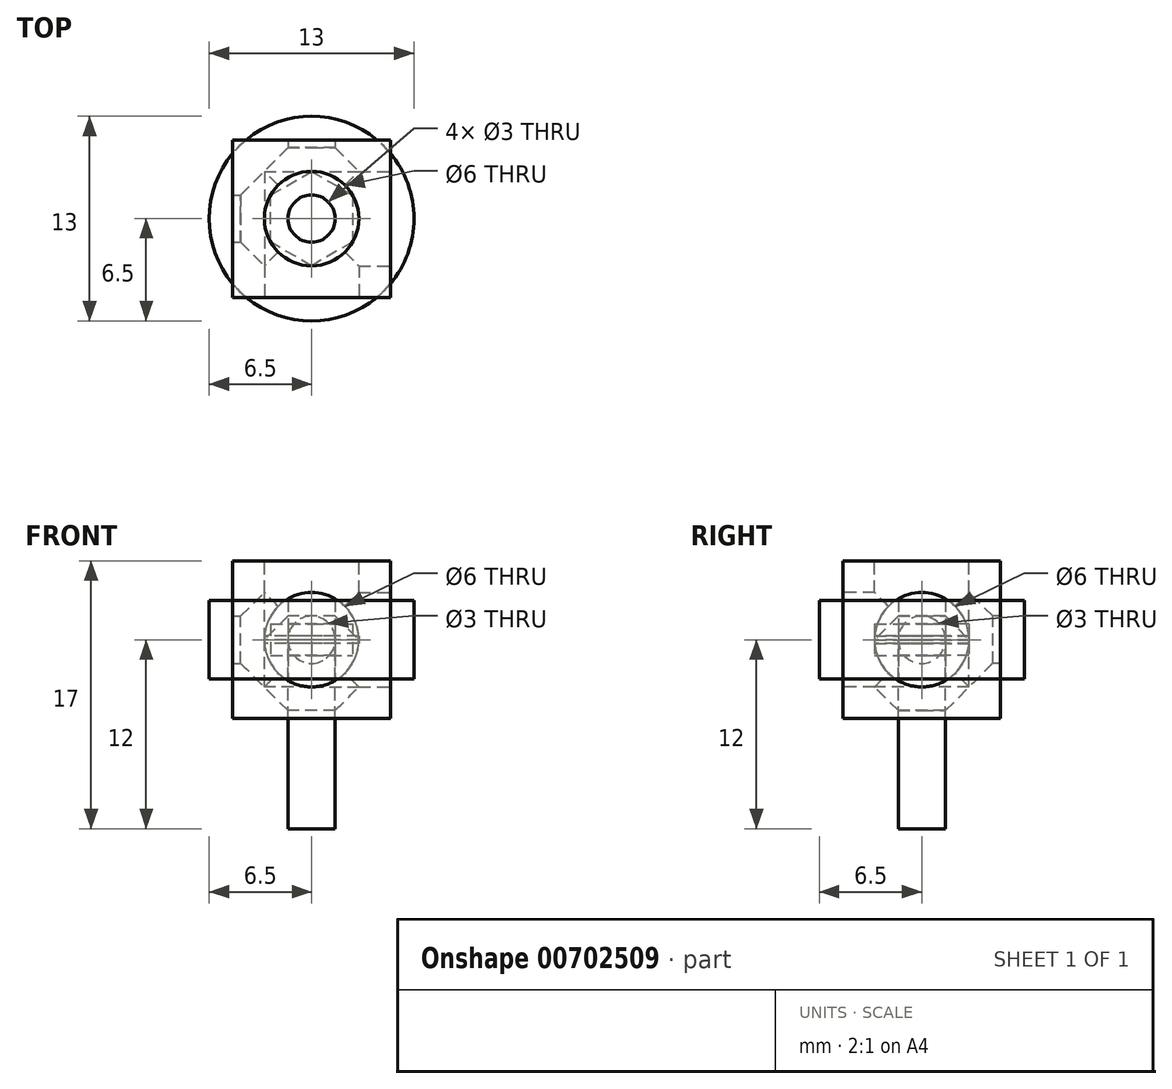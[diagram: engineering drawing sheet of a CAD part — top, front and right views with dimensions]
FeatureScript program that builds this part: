
annotation { "Feature Type Name" : "Feature", "Feature Type Description" : "" }
export const myFeature = defineFeature(function(context is Context, id is Id, definition is map)
    precondition{}
    {
        {
            var Q0;
            Q0=qCreatedBy(makeId("Top.planeOp"),FACE);
            var sketch = newSketch(context, id + "F0", { "sketchPlane" : qUnion([Q0])});
            skLineSegment(sketch, "E0.bottom", {"start": v(-5, 5) * mm, "end": v(5, 5) * mm});
            skLineSegment(sketch, "E0.top", {"start": v(-5, -5) * mm, "end": v(5, -5) * mm});
            skLineSegment(sketch, "E0.left", {"start": v(-5, 5) * mm, "end": v(-5, -5) * mm});
            skLineSegment(sketch, "E0.right", {"start": v(5, 5) * mm, "end": v(5, -5) * mm});
            skPoint(sketch, "E0.middle", {"position": v(0, 0) * mm});
            skSolve(sketch);
        }
        {
            var Q0;
            Q0=makeQuery(id+"F0.imprint","IMPRINT",FACE,{"disambiguationData":[TD([[makeQuery(id+"F0.imprint","IMPRINT",EDGE,{"derivedFrom":sQuery(id+"F0.wireOp",EDGE,"E0.bottom")}),-1.0]])]});
            extrude(context, id + "F1", {"entities" : qUnion([Q0]), "endBound" : BoundingType.SYMMETRIC, "depth" : 10 * mm, "offsetDistance" : 25 * mm});
        }
        {
            var Q0;
            Q0=makeQuery(id+"F1.opExtrude","SWEPT_FACE",FACE,{"disambiguationData":[OSD([sQuery(id+"F0.wireOp",EDGE,"E0.top")])]});
            var sketch = newSketch(context, id + "F2", { "sketchPlane" : qUnion([Q0])});
            skCircle(sketch, "E1", {"center": v(0, 0) * mm, "radius": 3 * mm});
            skCircle(sketch, "E2", {"center": v(0, 0) * mm, "radius": 1.5 * mm});
            skSolve(sketch);
        }
        {
            var Q0;
            Q0=makeQuery(id+"F2.imprint","IMPRINT",FACE,{"disambiguationData":[TD([[makeQuery(id+"F2.imprint","IMPRINT",EDGE,{"derivedFrom":sQuery(id+"F2.wireOp",EDGE,"E1")}),1.0]])]});
            var Q1;
            Q1=makeQuery(id+"F2.imprint","IMPRINT",FACE,{"disambiguationData":[TD([[makeQuery(id+"F2.imprint","IMPRINT",EDGE,{"derivedFrom":sQuery(id+"F2.wireOp",EDGE,"E2")}),1.0]])]});
            extrude(context, id + "F3", {"entities" : qUnion([Q0, Q1]), "operationType" : NewBodyOperationType.REMOVE, "oppositeDirection" : true, "depth" : 8 * mm, "offsetDistance" : 25 * mm});
        }
        {
            var Q0;
            Q0=makeQuery(id+"F1.opExtrude","SWEPT_FACE",FACE,{"disambiguationData":[OSD([sQuery(id+"F0.wireOp",EDGE,"E0.right")])]});
            var sketch = newSketch(context, id + "F4", { "sketchPlane" : qUnion([Q0])});
            skCircle(sketch, "E3", {"center": v(0, 0) * mm, "radius": 3 * mm});
            skCircle(sketch, "E4", {"center": v(0, 0) * mm, "radius": 1.5 * mm});
            skSolve(sketch);
        }
        {
            var Q0;
            Q0=makeQuery(id+"F4.imprint","IMPRINT",FACE,{"disambiguationData":[TD([[makeQuery(id+"F4.imprint","IMPRINT",EDGE,{"derivedFrom":sQuery(id+"F4.wireOp",EDGE,"E3")}),1.0]])]});
            var Q1;
            Q1=makeQuery(id+"F4.imprint","IMPRINT",FACE,{"disambiguationData":[TD([[makeQuery(id+"F4.imprint","IMPRINT",EDGE,{"derivedFrom":sQuery(id+"F4.wireOp",EDGE,"E4")}),1.0]])]});
            extrude(context, id + "F5", {"entities" : qUnion([Q0, Q1]), "operationType" : NewBodyOperationType.REMOVE, "oppositeDirection" : true, "depth" : 8 * mm, "offsetDistance" : 25 * mm});
        }
        {
            var Q0;
            Q0=makeQuery(id+"F1.opExtrude","CAP_FACE",FACE,{"disambiguationData":[OSD([sQuery(id+"F0.wireOp",EDGE,"E0.bottom"),sQuery(id+"F0.wireOp",EDGE,"E0.top"),sQuery(id+"F0.wireOp",EDGE,"E0.left"),sQuery(id+"F0.wireOp",EDGE,"E0.right")])],"isStart":false});
            var sketch = newSketch(context, id + "F6", { "sketchPlane" : qUnion([Q0])});
            skCircle(sketch, "E5", {"center": v(0, 0) * mm, "radius": 3 * mm});
            skCircle(sketch, "E6", {"center": v(0, 0) * mm, "radius": 1.5 * mm});
            skSolve(sketch);
        }
        {
            var Q0;
            Q0=makeQuery(id+"F6.imprint","IMPRINT",FACE,{"disambiguationData":[TD([[makeQuery(id+"F6.imprint","IMPRINT",EDGE,{"derivedFrom":sQuery(id+"F6.wireOp",EDGE,"E5")}),1.0]])]});
            var Q1;
            Q1=makeQuery(id+"F6.imprint","IMPRINT",FACE,{"disambiguationData":[TD([[makeQuery(id+"F6.imprint","IMPRINT",EDGE,{"derivedFrom":sQuery(id+"F6.wireOp",EDGE,"E6")}),1.0]])]});
            extrude(context, id + "F7", {"entities" : qUnion([Q0, Q1]), "operationType" : NewBodyOperationType.REMOVE, "oppositeDirection" : true, "depth" : 8 * mm, "offsetDistance" : 25 * mm});
        }
        {
            var Q0;
            Q0=makeQuery(id+"F2.imprint","IMPRINT",FACE,{"disambiguationData":[TD([[makeQuery(id+"F2.imprint","IMPRINT",EDGE,{"derivedFrom":sQuery(id+"F2.wireOp",EDGE,"E2")}),1.0]])]});
            extrude(context, id + "F8", {"entities" : qUnion([Q0]), "operationType" : NewBodyOperationType.REMOVE, "endBound" : BoundingType.THROUGH_ALL, "oppositeDirection" : true, "depth" : 25 * mm, "offsetDistance" : 25 * mm});
        }
        {
            var Q0;
            Q0=makeQuery(id+"F4.imprint","IMPRINT",FACE,{"disambiguationData":[TD([[makeQuery(id+"F4.imprint","IMPRINT",EDGE,{"derivedFrom":sQuery(id+"F4.wireOp",EDGE,"E4")}),1.0]])]});
            extrude(context, id + "F9", {"entities" : qUnion([Q0]), "operationType" : NewBodyOperationType.REMOVE, "endBound" : BoundingType.THROUGH_ALL, "oppositeDirection" : true, "depth" : 25 * mm, "offsetDistance" : 25 * mm});
        }
        {
            var Q0;
            Q0=makeQuery(id+"F6.imprint","IMPRINT",FACE,{"disambiguationData":[TD([[makeQuery(id+"F6.imprint","IMPRINT",EDGE,{"derivedFrom":sQuery(id+"F6.wireOp",EDGE,"E6")}),1.0]])]});
            extrude(context, id + "F10", {"entities" : qUnion([Q0]), "operationType" : NewBodyOperationType.REMOVE, "endBound" : BoundingType.THROUGH_ALL, "oppositeDirection" : true, "depth" : 25 * mm, "offsetDistance" : 25 * mm});
        }
        {
            var Q0;
            Q0=makeQuery(id+"F9.boolean.opBoolean","INTERSECT",EDGE,{"derivedFrom":[makeQuery(id+"F5.boolean.opBoolean","COPY",FACE,{"derivedFrom":makeQuery(id+"F5.opExtrude","CAP_FACE",FACE,{"disambiguationData":[OSD([sQuery(id+"F4.wireOp",EDGE,"E3")])],"isStart":false})}),makeQuery(id+"F9.opExtrude","SWEPT_FACE",FACE,{"disambiguationData":[OSD([sQuery(id+"F4.wireOp",EDGE,"E4")])]})]});
            var Q1;
            Q1=makeQuery(id+"F8.boolean.opBoolean","INTERSECT",EDGE,{"derivedFrom":[makeQuery(id+"F3.boolean.opBoolean","COPY",FACE,{"derivedFrom":makeQuery(id+"F3.opExtrude","CAP_FACE",FACE,{"disambiguationData":[OSD([sQuery(id+"F2.wireOp",EDGE,"E1")])],"isStart":false})}),makeQuery(id+"F8.opExtrude","SWEPT_FACE",FACE,{"disambiguationData":[OSD([sQuery(id+"F2.wireOp",EDGE,"E2")])]})]});
            var Q2;
            Q2=makeQuery(id+"F10.boolean.opBoolean","INTERSECT",EDGE,{"derivedFrom":[makeQuery(id+"F7.boolean.opBoolean","COPY",FACE,{"derivedFrom":makeQuery(id+"F7.opExtrude","CAP_FACE",FACE,{"disambiguationData":[OSD([sQuery(id+"F6.wireOp",EDGE,"E5")])],"isStart":false})}),makeQuery(id+"F10.opExtrude","SWEPT_FACE",FACE,{"disambiguationData":[OSD([sQuery(id+"F6.wireOp",EDGE,"E6")])]})]});
            chamfer(context, id + "F11", {"entities" : qUnion([Q0, Q1, Q2]), "width" : 1.5 * mm, "tangentPropagation" : true});
        }
        {
            var Q0;
            Q0=qCreatedBy(makeId("Front.planeOp"),FACE);
            var sketch = newSketch(context, id + "F12", { "sketchPlane" : qUnion([Q0])});
            skLineSegment(sketch, "E7", {"start": v(0, 1.5) * mm, "end": v(-1.5, 1.5) * mm});
            skLineSegment(sketch, "E8", {"start": v(-1.5, 1.5) * mm, "end": v(-3, 0) * mm});
            skLineSegment(sketch, "E9", {"start": v(-3, 0) * mm, "end": v(-1.5, 0) * mm});
            skLineSegment(sketch, "E10", {"start": v(-1.5, 0) * mm, "end": v(-1.5, -12) * mm});
            skLineSegment(sketch, "E11", {"start": v(-1.5, -12) * mm, "end": v(0, -12) * mm});
            skLineSegment(sketch, "E12", {"start": v(0, 1.5) * mm, "end": v(0, -12) * mm});
            skSolve(sketch);
        }
        {
            var Q0;
            Q0=makeQuery(id+"F12.imprint","IMPRINT",FACE,{"disambiguationData":[TD([[makeQuery(id+"F12.imprint","IMPRINT",EDGE,{"derivedFrom":sQuery(id+"F12.wireOp",EDGE,"E7")}),1.0]])]});
            var Q1;
            Q1=sQuery(id+"F12.wireOp",EDGE,"E12");
            revolve(context, id + "F13", {"entities" : qUnion([Q0]), "axis" : qUnion([Q1]), "revolveType" : RevolveType.FULL});
        }
        {
            var Q0;
            Q0=qCreatedBy(makeId("Top.planeOp"),FACE);
            var sketch = newSketch(context, id + "F14", { "sketchPlane" : qUnion([Q0])});
            skCircle(sketch, "E13", {"center": v(0, 0) * mm, "radius": 6.5 * mm});
            skCircle(sketch, "E14", {"center": v(0, 0) * mm, "radius": 1.5 * mm});
            skSolve(sketch);
        }
        {
            var Q0;
            Q0=makeQuery(id+"F14.imprint","IMPRINT",FACE,{"disambiguationData":[TD([[makeQuery(id+"F14.imprint","IMPRINT",EDGE,{"derivedFrom":sQuery(id+"F14.wireOp",EDGE,"E13")}),1.0]])]});
            extrude(context, id + "F15", {"entities" : qUnion([Q0]), "endBound" : BoundingType.SYMMETRIC, "depth" : 5 * mm, "offsetDistance" : 25 * mm});
        }
        {
            var Q0;
            Q0=qCreatedBy(makeId("Top.planeOp"),FACE);
            var sketch = newSketch(context, id + "F16", { "sketchPlane" : qUnion([Q0])});
            skCircle(sketch, "E15.cCircle", {"center": v(0, 0) * mm, "radius": 3 * mm, "construction": true});
            skLineSegment(sketch, "E15.0", {"start": v(0, 3) * mm, "end": v(2.6, 1.5) * mm});
            skLineSegment(sketch, "E15.1", {"start": v(2.6, 1.5) * mm, "end": v(2.6, -1.5) * mm});
            skLineSegment(sketch, "E15.2", {"start": v(2.6, -1.5) * mm, "end": v(0, -3) * mm});
            skLineSegment(sketch, "E15.3", {"start": v(0, -3) * mm, "end": v(-2.6, -1.5) * mm});
            skLineSegment(sketch, "E15.4", {"start": v(-2.6, -1.5) * mm, "end": v(-2.6, 1.5) * mm});
            skLineSegment(sketch, "E15.5", {"start": v(-2.6, 1.5) * mm, "end": v(0, 3) * mm});
            skCircle(sketch, "E16", {"center": v(0, 0) * mm, "radius": 1.5 * mm});
            skSolve(sketch);
        }
        {
            var Q0;
            Q0=qSketchRegion(id+"F16",true);
            extrude(context, id + "F17", {"entities" : qUnion([Q0]), "endBound" : BoundingType.SYMMETRIC, "depth" : 2 * mm, "offsetDistance" : 25 * mm});
        }
        {
            var Q0;
            Q0=qCreatedBy(makeId("Top.planeOp"),FACE);
            var sketch = newSketch(context, id + "F18", { "sketchPlane" : qUnion([Q0])});
            skCircle(sketch, "E17", {"center": v(0, 0) * mm, "radius": 1.5 * mm});
            skCircle(sketch, "E18", {"center": v(0, 0) * mm, "radius": 3 * mm});
            skSolve(sketch);
        }
        {
            var Q0;
            Q0=makeQuery(id+"F18.imprint","IMPRINT",FACE,{"disambiguationData":[TD([[makeQuery(id+"F18.imprint","IMPRINT",EDGE,{"derivedFrom":sQuery(id+"F18.wireOp",EDGE,"E17")}),-1.0]])]});
            extrude(context, id + "F19", {"entities" : qUnion([Q0]), "endBound" : BoundingType.SYMMETRIC, "depth" : 0.5 * mm, "offsetDistance" : 25 * mm});
        }
    });
